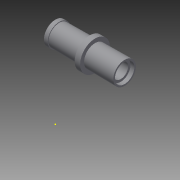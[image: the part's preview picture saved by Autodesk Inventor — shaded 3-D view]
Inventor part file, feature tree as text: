
AUTODESK INVENTOR PART (.ipt)
format: ipt  version: 2015 (Build 190159000, 159)  size: 117,248 bytes
history: native  units: in
note: dims shown in document units (in); Inventor stores cm internally (conversion verified against a paired STEP export)
features: sketch x2, revolve x1, plane x1
ambient origin geometry x8: Origin, YZ Plane, XZ Plane, XY Plane, X Axis, Y Axis, Z Axis, Center Point
bodies: Solid1 (feature_tree)
feature tree (4):
  revolve  "Revolution1"  [1 undecoded]
  plane  "Work Plane1"
  sketch  "Sketch5"
  sketch  "Sketch1"  dims[d55=90.0deg d56=0.0in]
note: 1 required parameter value undecoded (feature->parameter linkage not recoverable at this tier; creation-order binding heuristic only, values carry confidence <= 0.55)
